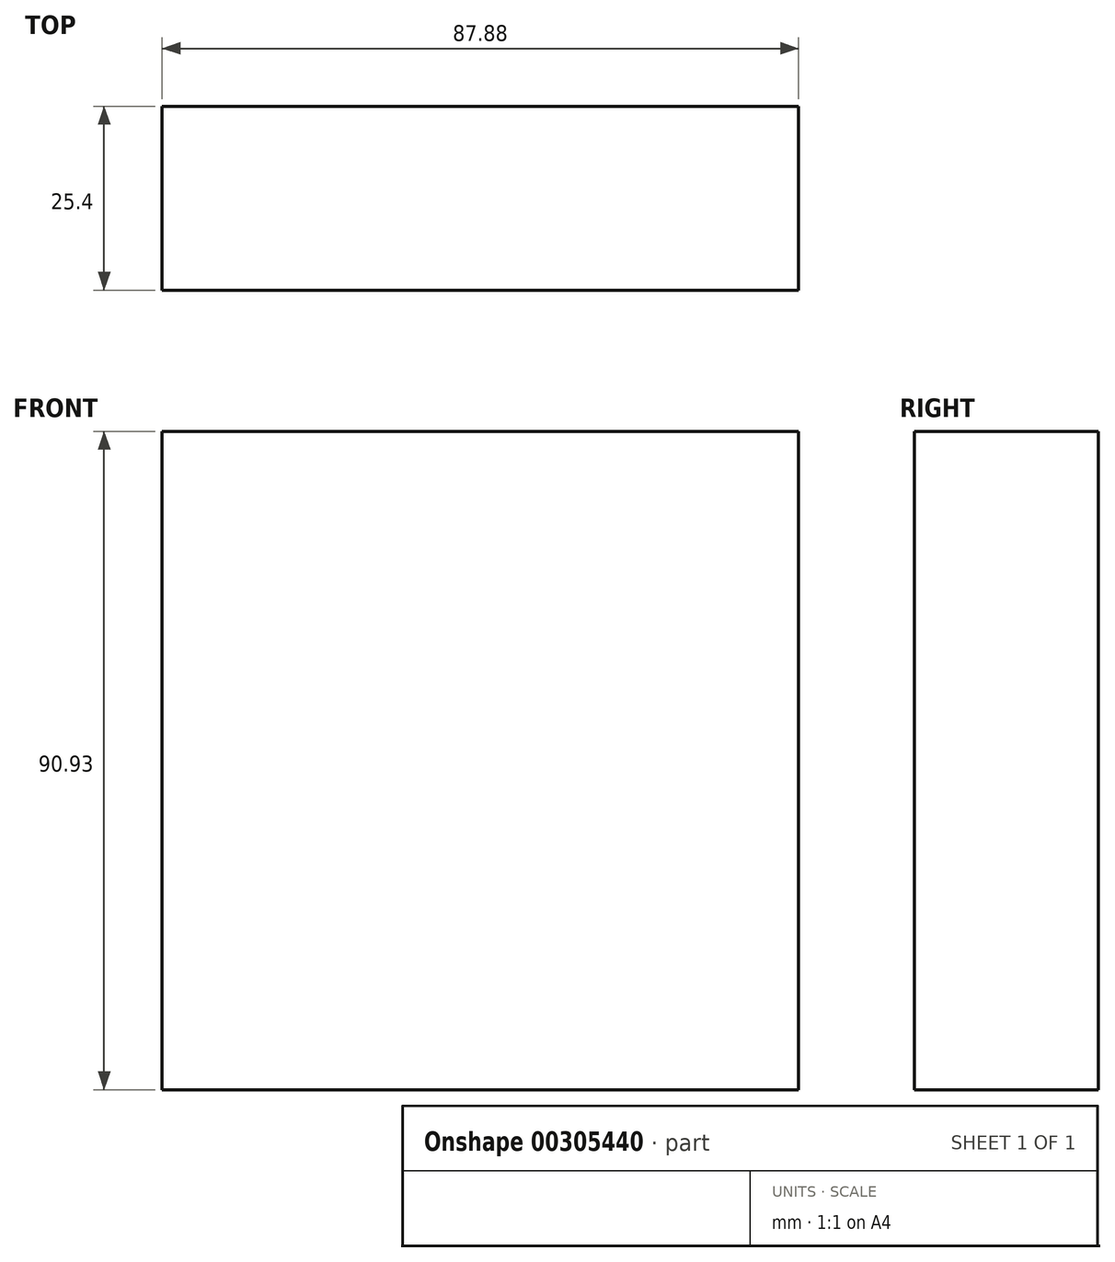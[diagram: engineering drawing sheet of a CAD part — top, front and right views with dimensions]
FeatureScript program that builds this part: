
annotation { "Feature Type Name" : "Feature", "Feature Type Description" : "" }
export const myFeature = defineFeature(function(context is Context, id is Id, definition is map)
    precondition{}
    {
        {
            var Q0;
            Q0=qCreatedBy(makeId("Front.planeOp"),FACE);
            var sketch = newSketch(context, id + "F0", { "sketchPlane" : qUnion([Q0])});
            skLineSegment(sketch, "E0.bottom", {"start": v(-45.65, 54.24) * mm, "end": v(42.23, 54.24) * mm});
            skLineSegment(sketch, "E0.top", {"start": v(-45.65, -36.69) * mm, "end": v(42.23, -36.69) * mm});
            skLineSegment(sketch, "E0.left", {"start": v(-45.65, 54.24) * mm, "end": v(-45.65, -36.69) * mm});
            skLineSegment(sketch, "E0.right", {"start": v(42.23, 54.24) * mm, "end": v(42.23, -36.69) * mm});
            skSolve(sketch);
        }
        {
            var Q0;
            Q0 = qSketchRegion(id + "F0", true);
            extrude(context, id + "F1", {"entities" : qUnion([Q0]), "depth" : 25.4 * mm});
        }
    });
